# Revit family: Lighting-UrbanLighting-GEWISS-EXTRO-SWIVEL_BRACKET
name_source: partatom
category: Apparecchi per illuminazione
units: mm (PartAtom-declared; Revit-internal decimal feet)

## family parameters
Condiviso = No
Host = Superficie
Punto di calcolo locali = Sì
Quota connettore circolare = Usa diametro
Sorgente d'illuminazione = No
Taglio con vuoti quando caricato = No
Tipo di parte = Normale

## types (1)
- GW82290 - SWIVEL BRACKET EXTRO G.GREY
    Catalogue = LIGHTING
    Colour = Graphite grey
    Descrizione = SWIVEL BRACKET EXTRO G.GREY
    Electrocod = 240
    IDF = ebd06d46-ea58-48f5-ae7e-d8e35020f21a
    IDT = 005f315cd5464f4fa58236bfda421664
    Immagine tipo = GW82290.jpg
    Material = Die-cast  aluminium
    Materiale elemento = Grigio grafite
    Modello = GW82290
    Outer dim. LxHxD (mm) = 140x120x100
    Produttore = GEWISS S.p.A.
    Prospetto di default = 1219 mm
    SEO = Swivel
    Technical sheet = https://www.gewiss.com
    URL = https://www.gewiss.com
    Version file RFA = 20.11
